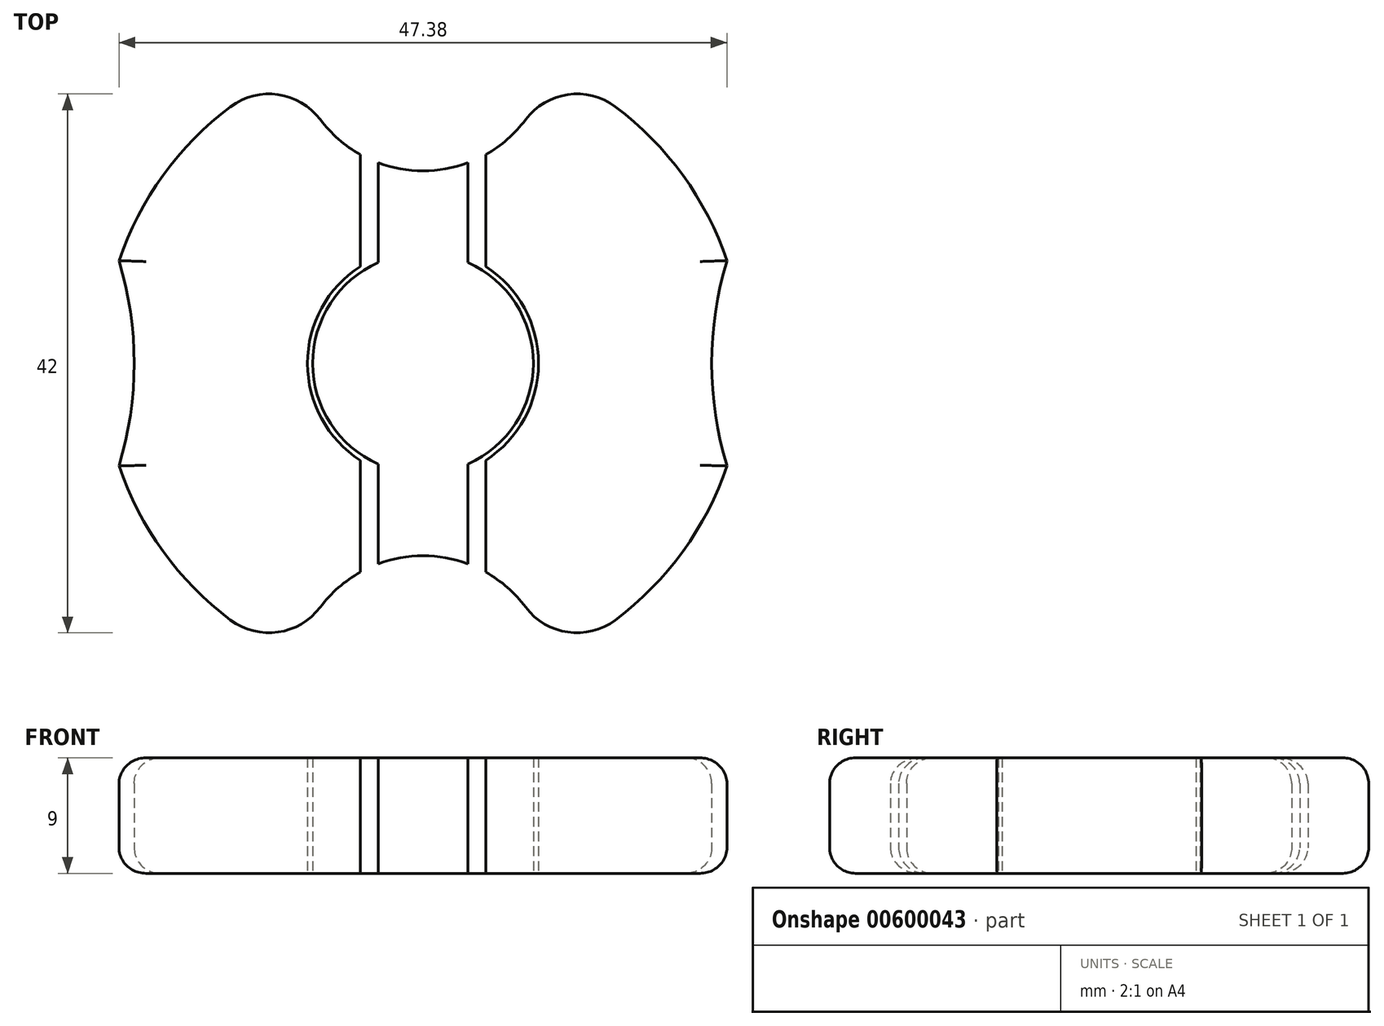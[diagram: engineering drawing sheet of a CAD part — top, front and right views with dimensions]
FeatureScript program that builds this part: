
annotation { "Feature Type Name" : "Feature", "Feature Type Description" : "" }
export const myFeature = defineFeature(function(context is Context, id is Id, definition is map)
    precondition{}
    {
        {
            var Q0;
            Q0=qCreatedBy(makeId("Top.planeOp"),FACE);
            var sketch = newSketch(context, id + "F0", { "sketchPlane" : qUnion([Q0])});
            skArc(sketch, "E0", {"start": v(3.5, -7.86) * mm, "mid": v(8.6, 0) * mm, "end": v(3.5, 7.86) * mm});
            skArc(sketch, "E1", {"start": v(-9.8, 23) * mm, "mid": v(-18.35, 16.98) * mm, "end": v(-23.69, 8) * mm});
            skArc(sketch, "E2", {"start": v(-9.8, 23) * mm, "mid": v(-8.07, 19.1) * mm, "end": v(-4.88, 16.27) * mm});
            skArc(sketch, "E3", {"start": v(9.8, -23) * mm, "mid": v(8.07, -19.1) * mm, "end": v(4.88, -16.27) * mm});
            skArc(sketch, "E4.trimOffspring", {"start": v(9.8, -23) * mm, "mid": v(18.35, -16.98) * mm, "end": v(23.69, -8) * mm});
            skArc(sketch, "E5", {"start": v(23.69, 8) * mm, "mid": v(22.5, 0) * mm, "end": v(23.69, -8) * mm});
            skArc(sketch, "E6.trimOffspring", {"start": v(23.69, 8) * mm, "mid": v(18.35, 16.98) * mm, "end": v(9.8, 23) * mm});
            skArc(sketch, "E7", {"start": v(-23.69, -8) * mm, "mid": v(-22.5, 0) * mm, "end": v(-23.69, 8) * mm});
            skArc(sketch, "E8.trimOffspring", {"start": v(-23.69, -8) * mm, "mid": v(-18.35, -16.98) * mm, "end": v(-9.8, -23) * mm});
            skLineSegment(sketch, "E9.left", {"start": v(-3.5, -15.63) * mm, "end": v(-3.5, -7.86) * mm});
            skLineSegment(sketch, "E9.right", {"start": v(3.5, -15.63) * mm, "end": v(3.5, -7.86) * mm});
            skLineSegment(sketch, "E10.left", {"start": v(-4.88, -16.27) * mm, "end": v(-4.88, -7.56) * mm});
            skLineSegment(sketch, "E10.right", {"start": v(4.88, -16.27) * mm, "end": v(4.88, -7.56) * mm});
            skPoint(sketch, "E11.orphan", {"position": v(4.88, 32.98) * mm});
            skPoint(sketch, "E12.orphan", {"position": v(-4.88, 32.98) * mm});
            skArc(sketch, "E13.trimOffspring", {"start": v(4.88, 16.27) * mm, "mid": v(8.07, 19.1) * mm, "end": v(9.8, 23) * mm});
            skArc(sketch, "E14.trimOffspring", {"start": v(-3.5, 15.63) * mm, "mid": v(0, 15) * mm, "end": v(3.5, 15.63) * mm});
            skPoint(sketch, "E15.orphan", {"position": v(4.88, -32.98) * mm});
            skPoint(sketch, "E16.orphan", {"position": v(-4.88, -32.98) * mm});
            skArc(sketch, "E17.trimOffspring", {"start": v(3.5, -15.63) * mm, "mid": v(0, -15) * mm, "end": v(-3.5, -15.63) * mm});
            skArc(sketch, "E18.trimOffspring", {"start": v(-4.88, -16.27) * mm, "mid": v(-8.07, -19.1) * mm, "end": v(-9.8, -23) * mm});
            skPoint(sketch, "E9.bottom.end.orphan", {"position": v(3.5, -29.75) * mm});
            skPoint(sketch, "E19.orphan", {"position": v(-3.5, -29.75) * mm});
            skPoint(sketch, "E9.top.end.orphan", {"position": v(3.5, 29.75) * mm});
            skPoint(sketch, "E20.orphan", {"position": v(-3.5, 29.75) * mm});
            skArc(sketch, "E21", {"start": v(4.88, -7.56) * mm, "mid": v(9, 0) * mm, "end": v(4.88, 7.56) * mm});
            skLineSegment(sketch, "E22.trimOffspring", {"start": v(4.88, 7.56) * mm, "end": v(4.88, 16.27) * mm});
            skArc(sketch, "E23.trimOffspring", {"start": v(-4.88, 7.56) * mm, "mid": v(-9, 0) * mm, "end": v(-4.88, -7.56) * mm});
            skLineSegment(sketch, "E24.trimOffspring", {"start": v(-4.88, 7.56) * mm, "end": v(-4.88, 16.27) * mm});
            skLineSegment(sketch, "E25.trimOffspring", {"start": v(-3.5, 7.86) * mm, "end": v(-3.5, 15.63) * mm});
            skLineSegment(sketch, "E26.trimOffspring", {"start": v(3.5, 7.86) * mm, "end": v(3.5, 15.63) * mm});
            skArc(sketch, "E27.trimOffspring", {"start": v(-3.5, 7.86) * mm, "mid": v(-8.6, 0) * mm, "end": v(-3.5, -7.86) * mm});
            skSolve(sketch);
        }
        {
            var Q0;
            Q0=makeQuery(id+"F0.imprint","IMPRINT",FACE,{"disambiguationData":[TD([[makeQuery(id+"F0.imprint","IMPRINT",EDGE,{"derivedFrom":sQuery(id+"F0.wireOp",EDGE,"E3")}),-1.0]])]});
            var Q1;
            Q1=makeQuery(id+"F0.imprint","IMPRINT",FACE,{"disambiguationData":[TD([[makeQuery(id+"F0.imprint","IMPRINT",EDGE,{"derivedFrom":sQuery(id+"F0.wireOp",EDGE,"E1")}),1.0]])]});
            var Q2;
            Q2=makeQuery(id+"F0.imprint","IMPRINT",FACE,{"disambiguationData":[TD([[makeQuery(id+"F0.imprint","IMPRINT",EDGE,{"derivedFrom":sQuery(id+"F0.wireOp",EDGE,"E0")}),1.0]])]});
            extrude(context, id + "F1", {"entities" : qUnion([Q0, Q1, Q2]), "depth" : 9 * mm, "offsetDistance" : 25 * mm});
        }
        {
            var Q0;
            Q0=makeQuery(id+"F1.opExtrude","CAP_EDGE",EDGE,{"disambiguationData":[OSD([sQuery(id+"F0.wireOp",EDGE,"E13.trimOffspring")])],"isStart":false});
            var Q1;
            Q1=makeQuery(id+"F1.opExtrude","CAP_EDGE",EDGE,{"disambiguationData":[OSD([sQuery(id+"F0.wireOp",EDGE,"E6.trimOffspring")])],"isStart":false});
            var Q2;
            Q2=makeQuery(id+"F1.opExtrude","CAP_EDGE",EDGE,{"disambiguationData":[OSD([sQuery(id+"F0.wireOp",EDGE,"E5")])],"isStart":false});
            var Q3;
            Q3=makeQuery(id+"F1.opExtrude","CAP_EDGE",EDGE,{"disambiguationData":[OSD([sQuery(id+"F0.wireOp",EDGE,"E4.trimOffspring")])],"isStart":false});
            var Q4;
            Q4=makeQuery(id+"F1.opExtrude","CAP_EDGE",EDGE,{"disambiguationData":[OSD([sQuery(id+"F0.wireOp",EDGE,"E3")])],"isStart":false});
            fillet(context, id + "F2", {"entities" : qUnion([Q0, Q1, Q2, Q3, Q4]), "radius" : 2 * mm, "tangentPropagation" : true, "allowEdgeOverflow" : false});
        }
        {
            var Q0;
            Q0=makeQuery(id+"F1.opExtrude","CAP_EDGE",EDGE,{"disambiguationData":[OSD([sQuery(id+"F0.wireOp",EDGE,"E2")])],"isStart":false});
            var Q1;
            Q1=makeQuery(id+"F1.opExtrude","CAP_EDGE",EDGE,{"disambiguationData":[OSD([sQuery(id+"F0.wireOp",EDGE,"E1")])],"isStart":false});
            var Q2;
            Q2=makeQuery(id+"F1.opExtrude","CAP_EDGE",EDGE,{"disambiguationData":[OSD([sQuery(id+"F0.wireOp",EDGE,"E7")])],"isStart":false});
            var Q3;
            Q3=makeQuery(id+"F1.opExtrude","CAP_EDGE",EDGE,{"disambiguationData":[OSD([sQuery(id+"F0.wireOp",EDGE,"E8.trimOffspring")])],"isStart":false});
            var Q4;
            Q4=makeQuery(id+"F1.opExtrude","CAP_EDGE",EDGE,{"disambiguationData":[OSD([sQuery(id+"F0.wireOp",EDGE,"E18.trimOffspring")])],"isStart":false});
            fillet(context, id + "F3", {"entities" : qUnion([Q0, Q1, Q2, Q3, Q4]), "radius" : 2 * mm, "tangentPropagation" : true, "allowEdgeOverflow" : false});
        }
        {
            var Q0;
            Q0=makeQuery(id+"F1.opExtrude","CAP_EDGE",EDGE,{"disambiguationData":[OSD([sQuery(id+"F0.wireOp",EDGE,"E17.trimOffspring")])],"isStart":false});
            var Q1;
            Q1=makeQuery(id+"F1.opExtrude","CAP_EDGE",EDGE,{"disambiguationData":[OSD([sQuery(id+"F0.wireOp",EDGE,"E14.trimOffspring")])],"isStart":false});
            fillet(context, id + "F4", {"entities" : qUnion([Q0, Q1]), "radius" : 2 * mm, "tangentPropagation" : true, "allowEdgeOverflow" : false});
        }
        {
            var Q0;
            Q0=makeQuery(id+"F2.opFillet","BLEND_EDGE",EDGE,{"blendedFrom":[makeQuery(id+"F1.opExtrude","CAP_EDGE",EDGE,{"disambiguationData":[OSD([sQuery(id+"F0.wireOp",EDGE,"E6.trimOffspring")])],"isStart":false}),makeQuery(id+"F1.opExtrude","CAP_EDGE",EDGE,{"disambiguationData":[OSD([sQuery(id+"F0.wireOp",EDGE,"E13.trimOffspring")])],"isStart":false})],"blendedInto":[]});
            var Q1;
            Q1=makeQuery(id+"F3.opFillet","BLEND_EDGE",EDGE,{"blendedFrom":[makeQuery(id+"F1.opExtrude","CAP_EDGE",EDGE,{"disambiguationData":[OSD([sQuery(id+"F0.wireOp",EDGE,"E1")])],"isStart":false}),makeQuery(id+"F1.opExtrude","CAP_EDGE",EDGE,{"disambiguationData":[OSD([sQuery(id+"F0.wireOp",EDGE,"E2")])],"isStart":false})],"blendedInto":[]});
            var Q2;
            Q2=makeQuery(id+"F2.opFillet","BLEND_EDGE",EDGE,{"blendedFrom":[makeQuery(id+"F1.opExtrude","CAP_EDGE",EDGE,{"disambiguationData":[OSD([sQuery(id+"F0.wireOp",EDGE,"E3")])],"isStart":false}),makeQuery(id+"F1.opExtrude","CAP_EDGE",EDGE,{"disambiguationData":[OSD([sQuery(id+"F0.wireOp",EDGE,"E4.trimOffspring")])],"isStart":false})],"blendedInto":[]});
            var Q3;
            Q3=makeQuery(id+"F3.opFillet","BLEND_EDGE",EDGE,{"blendedFrom":[makeQuery(id+"F1.opExtrude","CAP_EDGE",EDGE,{"disambiguationData":[OSD([sQuery(id+"F0.wireOp",EDGE,"E8.trimOffspring")])],"isStart":false}),makeQuery(id+"F1.opExtrude","CAP_EDGE",EDGE,{"disambiguationData":[OSD([sQuery(id+"F0.wireOp",EDGE,"E18.trimOffspring")])],"isStart":false})],"blendedInto":[]});
            fillet(context, id + "F5", {"entities" : qUnion([Q0, Q1, Q2, Q3]), "radius" : 5 * mm, "tangentPropagation" : true, "allowEdgeOverflow" : false});
        }
        {
            var Q0;
            Q0=makeQuery(id+"F1.opExtrude","CAP_EDGE",EDGE,{"disambiguationData":[OSD([sQuery(id+"F0.wireOp",EDGE,"E13.trimOffspring")])],"isStart":true});
            var Q1;
            {var subQ0=sQuery(id+"F0.wireOp",EDGE,"E13.trimOffspring");var subQ1=sQuery(id+"F0.wireOp",EDGE,"E6.trimOffspring");Q1=makeQuery(id+"F5.opFillet","BLEND_EDGE",EDGE,{"blendedFrom":[makeQuery(id+"F1.opExtrude","SWEPT_EDGE",EDGE,{"disambiguationData":[OSD([subQ1,subQ0])]}),makeQuery(id+"F1.opExtrude","CAP_FACE",FACE,{"disambiguationData":[OSD([sQuery(id+"F0.wireOp",EDGE,"E3"),sQuery(id+"F0.wireOp",EDGE,"E4.trimOffspring"),sQuery(id+"F0.wireOp",EDGE,"E5"),subQ1,sQuery(id+"F0.wireOp",EDGE,"E10.right"),subQ0,sQuery(id+"F0.wireOp",EDGE,"E21"),sQuery(id+"F0.wireOp",EDGE,"E22.trimOffspring")])],"isStart":true})],"blendedInto":[makeQuery(id+"F1.opExtrude","CAP_FACE",FACE,{"disambiguationData":[OSD([sQuery(id+"F0.wireOp",EDGE,"E3"),sQuery(id+"F0.wireOp",EDGE,"E4.trimOffspring"),sQuery(id+"F0.wireOp",EDGE,"E5"),subQ1,sQuery(id+"F0.wireOp",EDGE,"E10.right"),subQ0,sQuery(id+"F0.wireOp",EDGE,"E21"),sQuery(id+"F0.wireOp",EDGE,"E22.trimOffspring")])],"isStart":true})]});}
            var Q2;
            Q2=makeQuery(id+"F1.opExtrude","CAP_EDGE",EDGE,{"disambiguationData":[OSD([sQuery(id+"F0.wireOp",EDGE,"E6.trimOffspring")])],"isStart":true});
            var Q3;
            Q3=makeQuery(id+"F1.opExtrude","CAP_EDGE",EDGE,{"disambiguationData":[OSD([sQuery(id+"F0.wireOp",EDGE,"E5")])],"isStart":true});
            var Q4;
            Q4=makeQuery(id+"F1.opExtrude","CAP_EDGE",EDGE,{"disambiguationData":[OSD([sQuery(id+"F0.wireOp",EDGE,"E4.trimOffspring")])],"isStart":true});
            var Q5;
            {var subQ0=sQuery(id+"F0.wireOp",EDGE,"E4.trimOffspring");var subQ1=sQuery(id+"F0.wireOp",EDGE,"E3");Q5=makeQuery(id+"F5.opFillet","BLEND_EDGE",EDGE,{"blendedFrom":[makeQuery(id+"F1.opExtrude","SWEPT_EDGE",EDGE,{"disambiguationData":[OSD([subQ1,subQ0])]}),makeQuery(id+"F1.opExtrude","CAP_FACE",FACE,{"disambiguationData":[OSD([subQ1,subQ0,sQuery(id+"F0.wireOp",EDGE,"E5"),sQuery(id+"F0.wireOp",EDGE,"E6.trimOffspring"),sQuery(id+"F0.wireOp",EDGE,"E10.right"),sQuery(id+"F0.wireOp",EDGE,"E13.trimOffspring"),sQuery(id+"F0.wireOp",EDGE,"E21"),sQuery(id+"F0.wireOp",EDGE,"E22.trimOffspring")])],"isStart":true})],"blendedInto":[makeQuery(id+"F1.opExtrude","CAP_FACE",FACE,{"disambiguationData":[OSD([subQ1,subQ0,sQuery(id+"F0.wireOp",EDGE,"E5"),sQuery(id+"F0.wireOp",EDGE,"E6.trimOffspring"),sQuery(id+"F0.wireOp",EDGE,"E10.right"),sQuery(id+"F0.wireOp",EDGE,"E13.trimOffspring"),sQuery(id+"F0.wireOp",EDGE,"E21"),sQuery(id+"F0.wireOp",EDGE,"E22.trimOffspring")])],"isStart":true})]});}
            var Q6;
            Q6=makeQuery(id+"F1.opExtrude","CAP_EDGE",EDGE,{"disambiguationData":[OSD([sQuery(id+"F0.wireOp",EDGE,"E3")])],"isStart":true});
            fillet(context, id + "F6", {"entities" : qUnion([Q0, Q1, Q2, Q3, Q4, Q5, Q6]), "radius" : 2 * mm, "tangentPropagation" : true, "allowEdgeOverflow" : false});
        }
        {
            var Q0;
            Q0=makeQuery(id+"F1.opExtrude","CAP_EDGE",EDGE,{"disambiguationData":[OSD([sQuery(id+"F0.wireOp",EDGE,"E14.trimOffspring")])],"isStart":true});
            var Q1;
            Q1=makeQuery(id+"F1.opExtrude","CAP_EDGE",EDGE,{"disambiguationData":[OSD([sQuery(id+"F0.wireOp",EDGE,"E17.trimOffspring")])],"isStart":true});
            fillet(context, id + "F7", {"entities" : qUnion([Q0, Q1]), "radius" : 2 * mm, "tangentPropagation" : true, "allowEdgeOverflow" : false});
        }
        {
            var Q0;
            Q0=makeQuery(id+"F1.opExtrude","CAP_EDGE",EDGE,{"disambiguationData":[OSD([sQuery(id+"F0.wireOp",EDGE,"E2")])],"isStart":true});
            var Q1;
            {var subQ0=sQuery(id+"F0.wireOp",EDGE,"E2");var subQ1=sQuery(id+"F0.wireOp",EDGE,"E1");Q1=makeQuery(id+"F5.opFillet","BLEND_EDGE",EDGE,{"blendedFrom":[makeQuery(id+"F1.opExtrude","SWEPT_EDGE",EDGE,{"disambiguationData":[OSD([subQ1,subQ0])]}),makeQuery(id+"F1.opExtrude","CAP_FACE",FACE,{"disambiguationData":[OSD([subQ1,subQ0,sQuery(id+"F0.wireOp",EDGE,"E7"),sQuery(id+"F0.wireOp",EDGE,"E8.trimOffspring"),sQuery(id+"F0.wireOp",EDGE,"E10.left"),sQuery(id+"F0.wireOp",EDGE,"E18.trimOffspring"),sQuery(id+"F0.wireOp",EDGE,"E23.trimOffspring"),sQuery(id+"F0.wireOp",EDGE,"E24.trimOffspring")])],"isStart":true})],"blendedInto":[makeQuery(id+"F1.opExtrude","CAP_FACE",FACE,{"disambiguationData":[OSD([subQ1,subQ0,sQuery(id+"F0.wireOp",EDGE,"E7"),sQuery(id+"F0.wireOp",EDGE,"E8.trimOffspring"),sQuery(id+"F0.wireOp",EDGE,"E10.left"),sQuery(id+"F0.wireOp",EDGE,"E18.trimOffspring"),sQuery(id+"F0.wireOp",EDGE,"E23.trimOffspring"),sQuery(id+"F0.wireOp",EDGE,"E24.trimOffspring")])],"isStart":true})]});}
            var Q2;
            Q2=makeQuery(id+"F1.opExtrude","CAP_EDGE",EDGE,{"disambiguationData":[OSD([sQuery(id+"F0.wireOp",EDGE,"E1")])],"isStart":true});
            var Q3;
            Q3=makeQuery(id+"F1.opExtrude","CAP_EDGE",EDGE,{"disambiguationData":[OSD([sQuery(id+"F0.wireOp",EDGE,"E7")])],"isStart":true});
            var Q4;
            Q4=makeQuery(id+"F1.opExtrude","CAP_EDGE",EDGE,{"disambiguationData":[OSD([sQuery(id+"F0.wireOp",EDGE,"E8.trimOffspring")])],"isStart":true});
            var Q5;
            {var subQ0=sQuery(id+"F0.wireOp",EDGE,"E18.trimOffspring");var subQ1=sQuery(id+"F0.wireOp",EDGE,"E8.trimOffspring");Q5=makeQuery(id+"F5.opFillet","BLEND_EDGE",EDGE,{"blendedFrom":[makeQuery(id+"F1.opExtrude","SWEPT_EDGE",EDGE,{"disambiguationData":[OSD([subQ1,subQ0])]}),makeQuery(id+"F1.opExtrude","CAP_FACE",FACE,{"disambiguationData":[OSD([sQuery(id+"F0.wireOp",EDGE,"E1"),sQuery(id+"F0.wireOp",EDGE,"E2"),sQuery(id+"F0.wireOp",EDGE,"E7"),subQ1,sQuery(id+"F0.wireOp",EDGE,"E10.left"),subQ0,sQuery(id+"F0.wireOp",EDGE,"E23.trimOffspring"),sQuery(id+"F0.wireOp",EDGE,"E24.trimOffspring")])],"isStart":true})],"blendedInto":[makeQuery(id+"F1.opExtrude","CAP_FACE",FACE,{"disambiguationData":[OSD([sQuery(id+"F0.wireOp",EDGE,"E1"),sQuery(id+"F0.wireOp",EDGE,"E2"),sQuery(id+"F0.wireOp",EDGE,"E7"),subQ1,sQuery(id+"F0.wireOp",EDGE,"E10.left"),subQ0,sQuery(id+"F0.wireOp",EDGE,"E23.trimOffspring"),sQuery(id+"F0.wireOp",EDGE,"E24.trimOffspring")])],"isStart":true})]});}
            var Q6;
            Q6=makeQuery(id+"F1.opExtrude","CAP_EDGE",EDGE,{"disambiguationData":[OSD([sQuery(id+"F0.wireOp",EDGE,"E18.trimOffspring")])],"isStart":true});
            fillet(context, id + "F8", {"entities" : qUnion([Q0, Q1, Q2, Q3, Q4, Q5, Q6]), "radius" : 2 * mm, "tangentPropagation" : true, "allowEdgeOverflow" : false});
        }
    });
